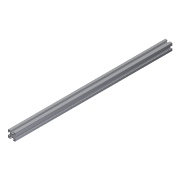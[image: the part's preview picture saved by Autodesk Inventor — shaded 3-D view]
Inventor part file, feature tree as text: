
AUTODESK INVENTOR PART (.ipt)
format: ipt  version: 2011 (Build 150239000, 239)  size: 168,960 bytes
history: native  units: in
note: dims shown in document units (in); Inventor stores cm internally (conversion verified against a paired STEP export)
features: extrude x1, sketch x1
ambient origin geometry x8: Origin, YZ Plane, XZ Plane, XY Plane, X Axis, Y Axis, Z Axis, Center Point
bodies: Solid1 (feature_tree)
feature tree (2):
  extrude  "Extrusion1"  [1 undecoded]
  sketch  "Sketch1"  dims[d0=16.7126in d1=0.0in]
note: 1 required parameter value undecoded (feature->parameter linkage not recoverable at this tier; creation-order binding heuristic only, values carry confidence <= 0.55)
